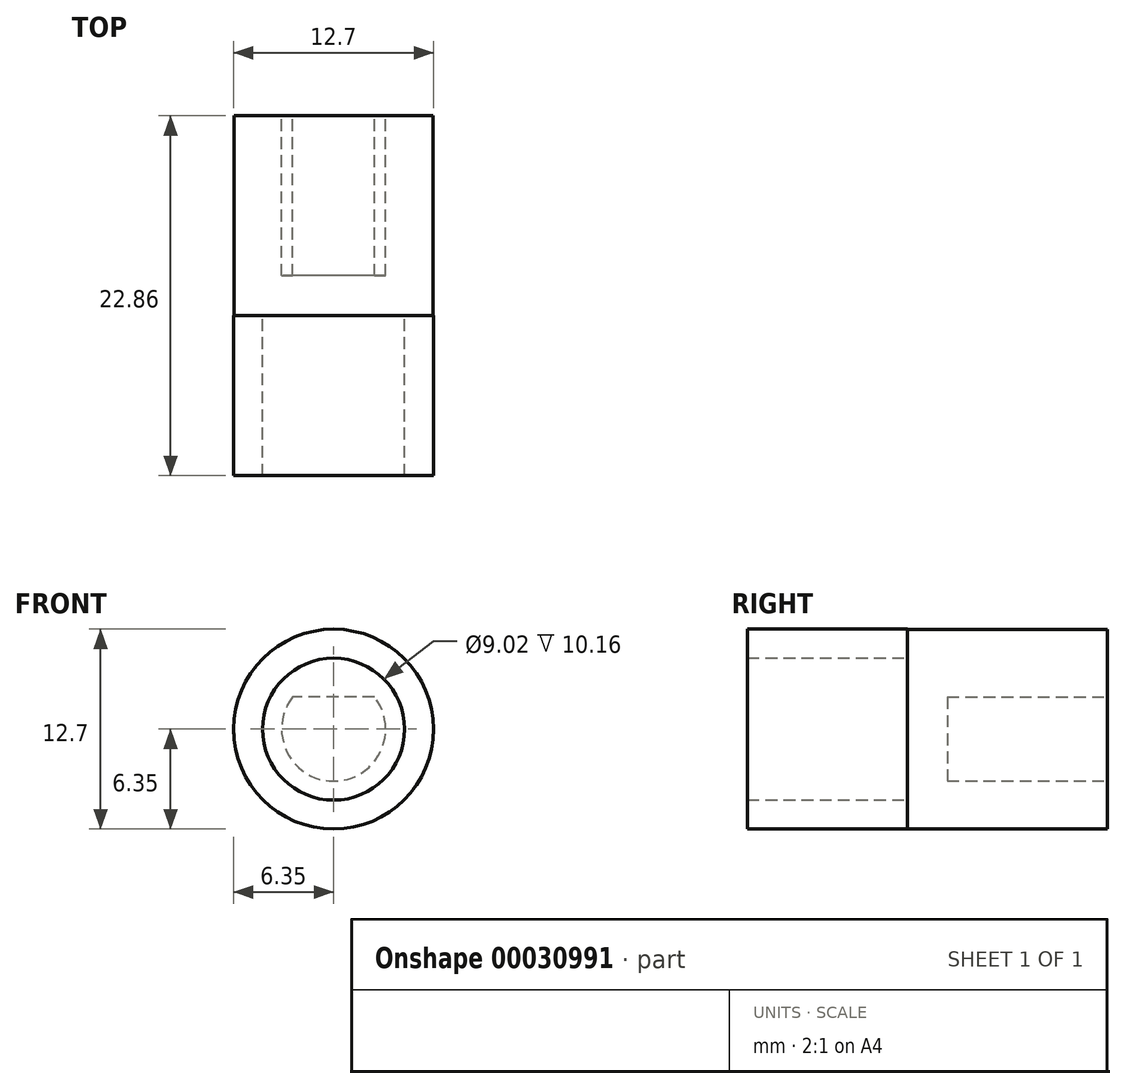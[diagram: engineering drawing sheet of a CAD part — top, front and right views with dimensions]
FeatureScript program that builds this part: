
annotation { "Feature Type Name" : "Feature", "Feature Type Description" : "" }
export const myFeature = defineFeature(function(context is Context, id is Id, definition is map)
    precondition{}
    {
        {
            var Q0;
            Q0=qCreatedBy(makeId("Front.planeOp"),FACE);
            var sketch = newSketch(context, id + "F0", { "sketchPlane" : qUnion([Q0])});
            skCircle(sketch, "E0", {"center": v(0, 0) * mm, "radius": 6.35 * mm});
            skCircle(sketch, "E1", {"center": v(0, 0) * mm, "radius": 4.5 * mm});
            skCircle(sketch, "E2.cCircle", {"center": v(0, 0) * mm, "radius": 4.5 * mm, "construction": true});
            skLineSegment(sketch, "E2.0", {"start": v(2.39, -3.82) * mm, "end": v(1.89, -4.1) * mm});
            skLineSegment(sketch, "E2.1", {"start": v(1.89, -4.1) * mm, "end": v(1.36, -4.3) * mm});
            skLineSegment(sketch, "E2.2", {"start": v(1.36, -4.3) * mm, "end": v(0.81, -4.43) * mm});
            skLineSegment(sketch, "E2.3", {"start": v(0.81, -4.43) * mm, "end": v(0.25, -4.5) * mm});
            skLineSegment(sketch, "E2.4", {"start": v(0.25, -4.5) * mm, "end": v(-0.32, -4.5) * mm});
            skLineSegment(sketch, "E2.5", {"start": v(-0.32, -4.5) * mm, "end": v(-0.88, -4.42) * mm});
            skLineSegment(sketch, "E2.6", {"start": v(-0.88, -4.42) * mm, "end": v(-1.42, -4.28) * mm});
            skLineSegment(sketch, "E2.7", {"start": v(-1.42, -4.28) * mm, "end": v(-1.95, -4.07) * mm});
            skLineSegment(sketch, "E2.8", {"start": v(-1.95, -4.07) * mm, "end": v(-2.44, -3.79) * mm});
            skLineSegment(sketch, "E2.9", {"start": v(-2.44, -3.79) * mm, "end": v(-2.9, -3.45) * mm});
            skLineSegment(sketch, "E2.10", {"start": v(-2.9, -3.45) * mm, "end": v(-3.3, -3.06) * mm});
            skLineSegment(sketch, "E2.11", {"start": v(-3.3, -3.06) * mm, "end": v(-3.67, -2.62) * mm});
            skLineSegment(sketch, "E2.12", {"start": v(-3.67, -2.62) * mm, "end": v(-3.97, -2.14) * mm});
            skLineSegment(sketch, "E2.13", {"start": v(-3.97, -2.14) * mm, "end": v(-4.2, -1.63) * mm});
            skLineSegment(sketch, "E2.14", {"start": v(-4.2, -1.63) * mm, "end": v(-4.37, -1.09) * mm});
            skLineSegment(sketch, "E2.15", {"start": v(-4.37, -1.09) * mm, "end": v(-4.48, -0.53) * mm});
            skLineSegment(sketch, "E2.16", {"start": v(-4.48, -0.53) * mm, "end": v(-4.5, 0.03) * mm});
            skLineSegment(sketch, "E2.17", {"start": v(-4.5, 0.03) * mm, "end": v(-4.47, 0.6) * mm});
            skLineSegment(sketch, "E2.18", {"start": v(-4.47, 0.6) * mm, "end": v(-4.36, 1.15) * mm});
            skLineSegment(sketch, "E2.19", {"start": v(-4.36, 1.15) * mm, "end": v(-4.18, 1.7) * mm});
            skLineSegment(sketch, "E2.20", {"start": v(-4.18, 1.7) * mm, "end": v(-3.93, 2.2) * mm});
            skLineSegment(sketch, "E2.21", {"start": v(-3.93, 2.2) * mm, "end": v(-3.63, 2.68) * mm});
            skLineSegment(sketch, "E2.22", {"start": v(-3.63, 2.68) * mm, "end": v(-3.26, 3.11) * mm});
            skLineSegment(sketch, "E2.23", {"start": v(-3.26, 3.11) * mm, "end": v(-2.85, 3.5) * mm});
            skLineSegment(sketch, "E2.24", {"start": v(-2.85, 3.5) * mm, "end": v(-2.39, 3.82) * mm});
            skLineSegment(sketch, "E2.25", {"start": v(-2.39, 3.82) * mm, "end": v(-1.89, 4.1) * mm});
            skLineSegment(sketch, "E2.26", {"start": v(-1.89, 4.1) * mm, "end": v(-1.36, 4.3) * mm});
            skLineSegment(sketch, "E2.27", {"start": v(-1.36, 4.3) * mm, "end": v(-0.81, 4.43) * mm});
            skLineSegment(sketch, "E2.28", {"start": v(-0.81, 4.43) * mm, "end": v(-0.25, 4.5) * mm});
            skLineSegment(sketch, "E2.29", {"start": v(-0.25, 4.5) * mm, "end": v(0.32, 4.5) * mm});
            skLineSegment(sketch, "E2.30", {"start": v(0.32, 4.5) * mm, "end": v(0.88, 4.42) * mm});
            skLineSegment(sketch, "E2.31", {"start": v(0.88, 4.42) * mm, "end": v(1.42, 4.28) * mm});
            skLineSegment(sketch, "E2.32", {"start": v(1.42, 4.28) * mm, "end": v(1.95, 4.07) * mm});
            skLineSegment(sketch, "E2.33", {"start": v(1.95, 4.07) * mm, "end": v(2.44, 3.79) * mm});
            skLineSegment(sketch, "E2.34", {"start": v(2.44, 3.79) * mm, "end": v(2.9, 3.45) * mm});
            skLineSegment(sketch, "E2.35", {"start": v(2.9, 3.45) * mm, "end": v(3.3, 3.06) * mm});
            skLineSegment(sketch, "E2.36", {"start": v(3.3, 3.06) * mm, "end": v(3.67, 2.62) * mm});
            skLineSegment(sketch, "E2.37", {"start": v(3.67, 2.62) * mm, "end": v(3.97, 2.14) * mm});
            skLineSegment(sketch, "E2.38", {"start": v(3.97, 2.14) * mm, "end": v(4.2, 1.63) * mm});
            skLineSegment(sketch, "E2.39", {"start": v(4.2, 1.63) * mm, "end": v(4.37, 1.09) * mm});
            skLineSegment(sketch, "E2.40", {"start": v(4.37, 1.09) * mm, "end": v(4.48, 0.53) * mm});
            skLineSegment(sketch, "E2.41", {"start": v(4.48, 0.53) * mm, "end": v(4.5, -0.03) * mm});
            skLineSegment(sketch, "E2.42", {"start": v(4.5, -0.03) * mm, "end": v(4.47, -0.6) * mm});
            skLineSegment(sketch, "E2.43", {"start": v(4.47, -0.6) * mm, "end": v(4.36, -1.15) * mm});
            skLineSegment(sketch, "E2.44", {"start": v(4.36, -1.15) * mm, "end": v(4.18, -1.7) * mm});
            skLineSegment(sketch, "E2.45", {"start": v(4.18, -1.7) * mm, "end": v(3.93, -2.2) * mm});
            skLineSegment(sketch, "E2.46", {"start": v(3.93, -2.2) * mm, "end": v(3.63, -2.68) * mm});
            skLineSegment(sketch, "E2.47", {"start": v(3.63, -2.68) * mm, "end": v(3.26, -3.11) * mm});
            skLineSegment(sketch, "E2.48", {"start": v(3.26, -3.11) * mm, "end": v(2.85, -3.5) * mm});
            skLineSegment(sketch, "E2.49", {"start": v(2.85, -3.5) * mm, "end": v(2.39, -3.82) * mm});
            skSolve(sketch);
        }
        {
            var Q0;
            Q0=makeQuery(id+"F0.imprint","IMPRINT",FACE,{"disambiguationData":[TD([[makeQuery(id+"F0.imprint","IMPRINT",EDGE,{"derivedFrom":sQuery(id+"F0.wireOp",EDGE,"E0")}),1.0]])]});
            extrude(context, id + "F1", {"entities" : qUnion([Q0]), "depth" : 10.16 * mm});
        }
        {
            var Q0;
            Q0=qCreatedBy(makeId("Front.planeOp"),FACE);
            var sketch = newSketch(context, id + "F2", { "sketchPlane" : qUnion([Q0])});
            skCircle(sketch, "E3", {"center": v(0, 0) * mm, "radius": 6.32 * mm});
            skSolve(sketch);
        }
        {
            var Q0;
            Q0 = qSketchRegion(id + "F2", true);
            extrude(context, id + "F3", {"entities" : qUnion([Q0]), "operationType" : NewBodyOperationType.ADD, "oppositeDirection" : true, "depth" : 12.7 * mm});
        }
        {
            var Q0;
            Q0=makeQuery(id+"F3.opExtrude","CAP_FACE",FACE,{"disambiguationData":[OSD([sQuery(id+"F2.wireOp",EDGE,"E3")])],"isStart":false});
            var sketch = newSketch(context, id + "F4", { "sketchPlane" : qUnion([Q0])});
            skCircle(sketch, "E4", {"center": v(0, 0) * mm, "radius": 3.3 * mm});
            skLineSegment(sketch, "E5", {"start": v(-2.6, 2.03) * mm, "end": v(2.6, 2.03) * mm});
            skSolve(sketch);
        }
        {
            var Q0;
            {var subQ0=sQuery(id+"F4.wireOp",EDGE,"E5");Q0=makeQuery(id+"F4.imprint","IMPRINT",FACE,{"disambiguationData":[TD([[makeQuery(id+"F4.imprint","IMPRINT",EDGE,{"derivedFrom":subQ0}),-1.0]])]});}
            extrude(context, id + "F5", {"entities" : qUnion([Q0]), "operationType" : NewBodyOperationType.REMOVE, "oppositeDirection" : true, "depth" : 10.16 * mm});
        }
        {
            var Q0;
            Q0=makeQuery(id+"F3.opExtrude","CAP_FACE",FACE,{"disambiguationData":[OSD([sQuery(id+"F2.wireOp",EDGE,"E3")])],"isStart":false});
            var sketch = newSketch(context, id + "F6", { "sketchPlane" : qUnion([Q0])});
            skCircle(sketch, "E6", {"center": v(0, 0) * mm, "radius": 3.56 * mm});
            skCircle(sketch, "E7", {"center": v(-0.33, 0) * mm, "radius": 8.83 * mm});
            skCircle(sketch, "E8", {"center": v(0, 0) * mm, "radius": 3.3 * mm});
            skLineSegment(sketch, "E9", {"start": v(2.6, 2.03) * mm, "end": v(-2.6, 2.03) * mm});
            skSolve(sketch);
        }
        {
            var Q0;
            Q0=makeQuery(id+"F6.imprint","IMPRINT",FACE,{"disambiguationData":[TD([[makeQuery(id+"F6.imprint","IMPRINT",EDGE,{"derivedFrom":sQuery(id+"F6.wireOp",EDGE,"E6")}),-1.0]])]});
            var Q1;
            {var subQ0=sQuery(id+"F6.wireOp",EDGE,"E9");Q1=makeQuery(id+"F6.imprint","IMPRINT",FACE,{"disambiguationData":[TD([[makeQuery(id+"F6.imprint","IMPRINT",EDGE,{"derivedFrom":subQ0}),1.0]])]});}
            extrude(context, id + "F7", {"entities" : qUnion([Q0, Q1]), "operationType" : NewBodyOperationType.ADD, "oppositeDirection" : true, "depth" : 12.7 * mm});
        }
    });
